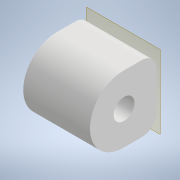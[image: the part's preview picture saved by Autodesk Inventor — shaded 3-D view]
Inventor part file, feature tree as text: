
AUTODESK INVENTOR PART (.ipt)
format: ipt  version: 2021 (Build 250183000, 183)  size: 116,224 bytes
history: native  units: mm
features: extrude x2, fillet x2, sketch x2
ambient origin geometry x8: Origin, YZ Plane, XZ Plane, XY Plane, X Axis, Y Axis, Z Axis, Center Point
bodies: Body1 (feature_tree)
feature tree (6):
  extrude  "Wyciągnięcie proste3"  Depth=80.0mm
  fillet  "Zaokrąglenie2"  Radius=80.0mm
  fillet  "Zaokrąglenie3"  Radius=80.0mm
  extrude  "Wyciągnięcie proste4"  Depth=18.0mm
  sketch  "Szkic3"
  sketch  "Szkic4"
